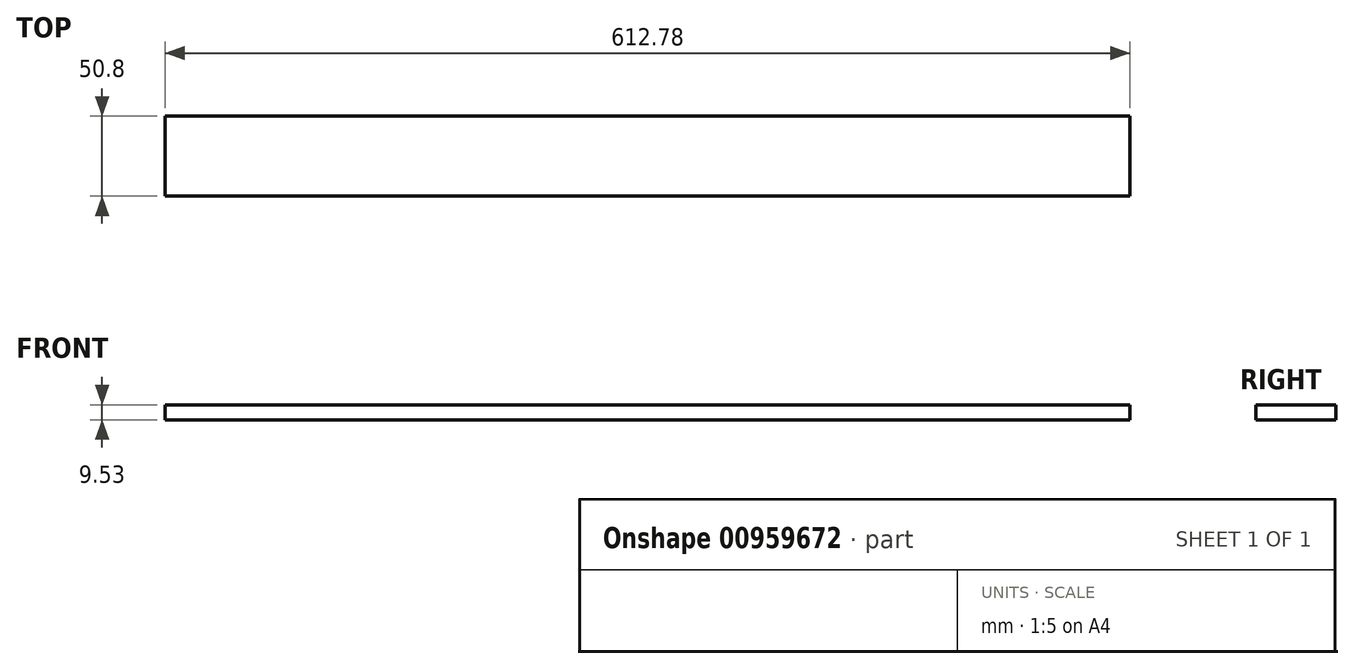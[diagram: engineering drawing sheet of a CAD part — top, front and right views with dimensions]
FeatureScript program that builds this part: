
annotation { "Feature Type Name" : "Feature", "Feature Type Description" : "" }
export const myFeature = defineFeature(function(context is Context, id is Id, definition is map)
    precondition{}
    {
        {
            var Q0;
            Q0=qCreatedBy(makeId("Top.planeOp"),FACE);
            var sketch = newSketch(context, id + "F0", { "sketchPlane" : qUnion([Q0])});
            skLineSegment(sketch, "E0.bottom", {"start": v(-57.4, 38.74) * mm, "end": v(555.38, 38.74) * mm});
            skLineSegment(sketch, "E0.top", {"start": v(-57.4, -12.06) * mm, "end": v(555.38, -12.06) * mm});
            skLineSegment(sketch, "E0.left", {"start": v(-57.4, 38.74) * mm, "end": v(-57.4, -12.06) * mm});
            skLineSegment(sketch, "E0.right", {"start": v(555.38, 38.74) * mm, "end": v(555.38, -12.06) * mm});
            skSolve(sketch);
        }
        {
            var Q0;
            Q0=makeQuery(id+"F0.imprint","IMPRINT",FACE,{"disambiguationData":[TD([[makeQuery(id+"F0.imprint","IMPRINT",EDGE,{"derivedFrom":sQuery(id+"F0.wireOp",EDGE,"E0.bottom")}),-1.0]])]});
            extrude(context, id + "F1", {"entities" : qUnion([Q0]), "depth" : 9.52 * mm, "offsetDistance" : 25.4 * mm});
        }
    });
